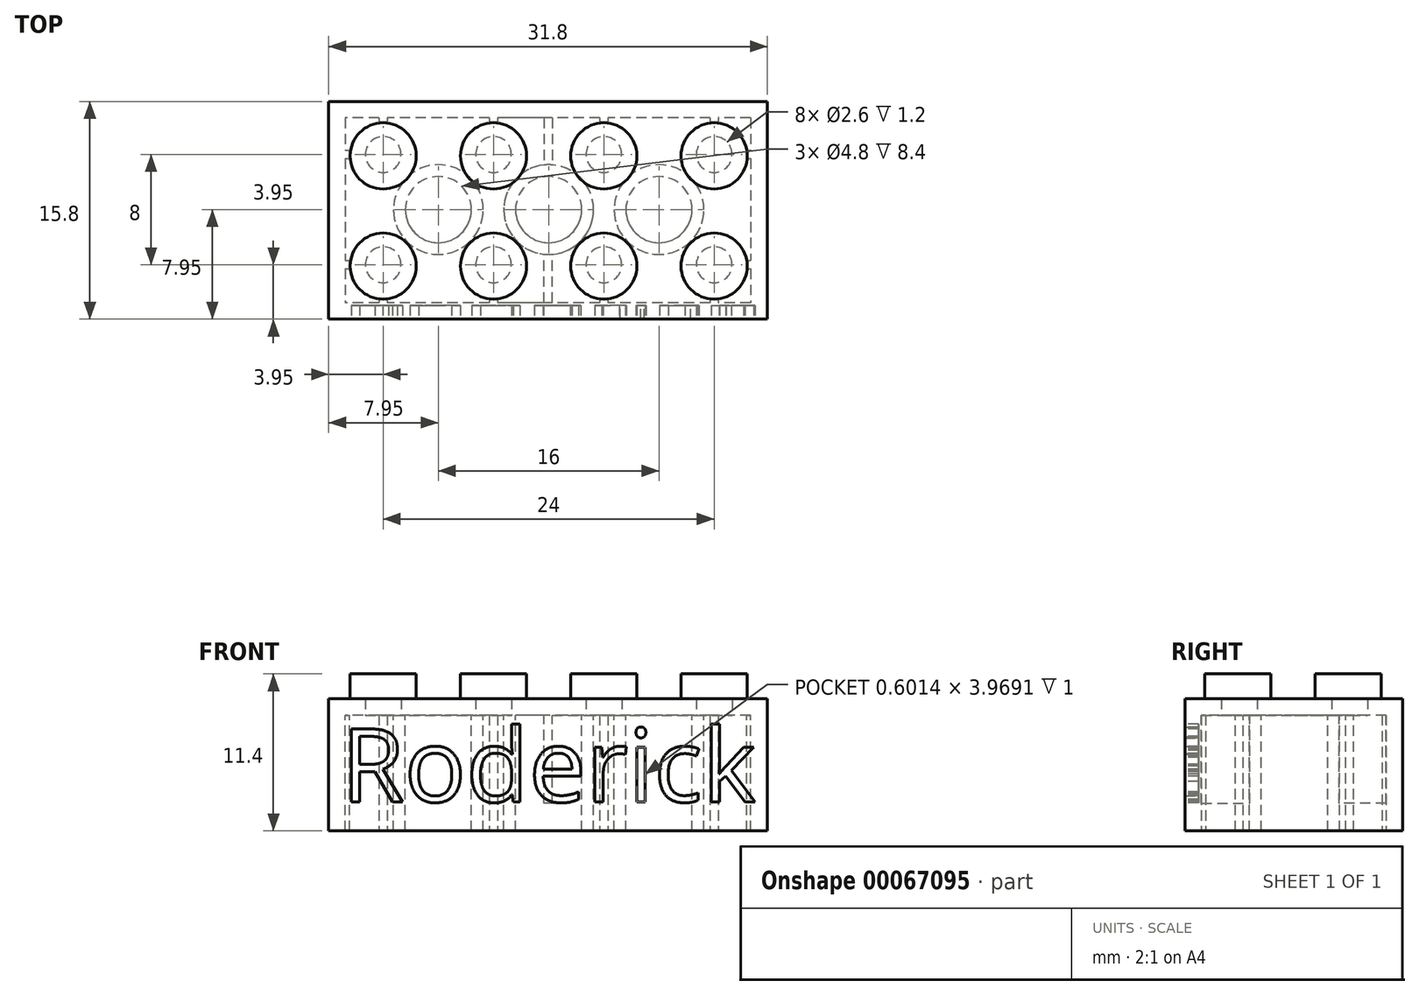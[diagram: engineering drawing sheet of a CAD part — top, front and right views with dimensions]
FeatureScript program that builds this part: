
annotation { "Feature Type Name" : "Feature", "Feature Type Description" : "" }
export const myFeature = defineFeature(function(context is Context, id is Id, definition is map)
    precondition{}
    {
        {
            var Q0;
            Q0=qCreatedBy(makeId("Top.planeOp"),FACE);
            var sketch = newSketch(context, id + "F0", { "sketchPlane" : qUnion([Q0])});
            skLineSegment(sketch, "E0.rect.bottom", {"start": v(15.9, -7.9) * mm, "end": v(-15.9, -7.9) * mm});
            skLineSegment(sketch, "E0.rect.top", {"start": v(15.9, 7.9) * mm, "end": v(-15.9, 7.9) * mm});
            skLineSegment(sketch, "E0.rect.left", {"start": v(15.9, -7.9) * mm, "end": v(15.9, 7.9) * mm});
            skLineSegment(sketch, "E0.rect.right", {"start": v(-15.9, -7.9) * mm, "end": v(-15.9, 7.9) * mm});
            skPoint(sketch, "E0.rect.middle", {"position": v(0, 0) * mm});
            skSolve(sketch);
        }
        {
            var Q0;
            Q0 = qSketchRegion(id + "F0", true);
            extrude(context, id + "F1", {"entities" : qUnion([Q0]), "depth" : 9.6 * mm});
        }
        {
            var Q0;
            Q0=makeQuery(id+"F1.opExtrude","CAP_FACE",FACE,{"disambiguationData":[OSD([sQuery(id+"F0.wireOp",EDGE,"E0.rect.bottom"),sQuery(id+"F0.wireOp",EDGE,"E0.rect.top"),sQuery(id+"F0.wireOp",EDGE,"E0.rect.left"),sQuery(id+"F0.wireOp",EDGE,"E0.rect.right")])],"isStart":true});
            var sketch = newSketch(context, id + "F2", { "sketchPlane" : qUnion([Q0])});
            skLineSegment(sketch, "E1.rect.bottom", {"start": v(14.7, -6.7) * mm, "end": v(-14.7, -6.7) * mm});
            skLineSegment(sketch, "E1.rect.top", {"start": v(14.7, 6.7) * mm, "end": v(-14.7, 6.7) * mm});
            skLineSegment(sketch, "E1.rect.left", {"start": v(14.7, -6.7) * mm, "end": v(14.7, 6.7) * mm});
            skLineSegment(sketch, "E1.rect.right", {"start": v(-14.7, -6.7) * mm, "end": v(-14.7, 6.7) * mm});
            skPoint(sketch, "E1.rect.middle", {"position": v(0, 0) * mm});
            skSolve(sketch);
        }
        {
            var Q0;
            Q0 = qSketchRegion(id + "F2", true);
            var Q1;
            Q1 = qSketchRegion(id + "F8", true);
            extrude(context, id + "F3", {"entities" : qUnion([Q0, Q1]), "operationType" : NewBodyOperationType.REMOVE, "oppositeDirection" : true, "depth" : 8.4 * mm});
        }
        {
            var Q0;
            Q0=makeQuery(id+"F1.opExtrude","CAP_FACE",FACE,{"disambiguationData":[OSD([sQuery(id+"F0.wireOp",EDGE,"E0.rect.bottom"),sQuery(id+"F0.wireOp",EDGE,"E0.rect.top"),sQuery(id+"F0.wireOp",EDGE,"E0.rect.left"),sQuery(id+"F0.wireOp",EDGE,"E0.rect.right")])],"isStart":false});
            var sketch = newSketch(context, id + "F4", { "sketchPlane" : qUnion([Q0])});
            skLineSegment(sketch, "E2", {"start": v(-30.02, 0) * mm, "end": v(25.7, 0) * mm, "construction": true});
            skCircle(sketch, "E3", {"center": v(-11.95, 3.95) * mm, "radius": 2.4 * mm});
            skCircle(sketch, "E4.0.1.0", {"center": v(-11.95, -4.05) * mm, "radius": 2.4 * mm});
            skCircle(sketch, "E4.1.0.0", {"center": v(-3.95, 3.95) * mm, "radius": 2.4 * mm});
            skCircle(sketch, "E4.1.1.0", {"center": v(-3.95, -4.05) * mm, "radius": 2.4 * mm});
            skCircle(sketch, "E4.2.0.0", {"center": v(4.05, 3.95) * mm, "radius": 2.4 * mm});
            skCircle(sketch, "E4.2.1.0", {"center": v(4.05, -4.05) * mm, "radius": 2.4 * mm});
            skCircle(sketch, "E4.3.0.0", {"center": v(12.05, 3.95) * mm, "radius": 2.4 * mm});
            skCircle(sketch, "E4.3.1.0", {"center": v(12.05, -4.05) * mm, "radius": 2.4 * mm});
            skLineSegment(sketch, "E4.direction1", {"start": v(-11.95, 3.95) * mm, "end": v(-3.95, 3.95) * mm, "construction": true});
            skLineSegment(sketch, "E4.direction2", {"start": v(-11.95, 3.95) * mm, "end": v(-11.95, -4.05) * mm, "construction": true});
            skSolve(sketch);
        }
        {
            var Q0;
            Q0=makeQuery(id+"F4.imprint","IMPRINT",FACE,{"disambiguationData":[TD([[makeQuery(id+"F4.imprint","IMPRINT",EDGE,{"derivedFrom":sQuery(id+"F4.wireOp",EDGE,"E3")}),1.0]])]});
            var Q1;
            Q1=makeQuery(id+"F4.imprint","IMPRINT",FACE,{"disambiguationData":[TD([[makeQuery(id+"F4.imprint","IMPRINT",EDGE,{"derivedFrom":sQuery(id+"F4.wireOp",EDGE,"E4.1.0.0")}),1.0]])]});
            var Q2;
            Q2=makeQuery(id+"F4.imprint","IMPRINT",FACE,{"disambiguationData":[TD([[makeQuery(id+"F4.imprint","IMPRINT",EDGE,{"derivedFrom":sQuery(id+"F4.wireOp",EDGE,"E4.2.0.0")}),1.0]])]});
            var Q3;
            Q3=makeQuery(id+"F4.imprint","IMPRINT",FACE,{"disambiguationData":[TD([[makeQuery(id+"F4.imprint","IMPRINT",EDGE,{"derivedFrom":sQuery(id+"F4.wireOp",EDGE,"E4.3.0.0")}),1.0]])]});
            var Q4;
            Q4=makeQuery(id+"F4.imprint","IMPRINT",FACE,{"disambiguationData":[TD([[makeQuery(id+"F4.imprint","IMPRINT",EDGE,{"derivedFrom":sQuery(id+"F4.wireOp",EDGE,"E4.3.1.0")}),1.0]])]});
            var Q5;
            Q5=makeQuery(id+"F4.imprint","IMPRINT",FACE,{"disambiguationData":[TD([[makeQuery(id+"F4.imprint","IMPRINT",EDGE,{"derivedFrom":sQuery(id+"F4.wireOp",EDGE,"E4.2.1.0")}),1.0]])]});
            var Q6;
            Q6=makeQuery(id+"F4.imprint","IMPRINT",FACE,{"disambiguationData":[TD([[makeQuery(id+"F4.imprint","IMPRINT",EDGE,{"derivedFrom":sQuery(id+"F4.wireOp",EDGE,"E4.1.1.0")}),1.0]])]});
            var Q7;
            Q7=makeQuery(id+"F4.imprint","IMPRINT",FACE,{"disambiguationData":[TD([[makeQuery(id+"F4.imprint","IMPRINT",EDGE,{"derivedFrom":sQuery(id+"F4.wireOp",EDGE,"E4.0.1.0")}),1.0]])]});
            extrude(context, id + "F5", {"entities" : qUnion([Q0, Q1, Q2, Q3, Q4, Q5, Q6, Q7]), "operationType" : NewBodyOperationType.ADD, "depth" : 1.8 * mm});
        }
        {
            var Q0;
            Q0=makeQuery(id+"F3.boolean.opBoolean","COPY",FACE,{"derivedFrom":makeQuery(id+"F3.opExtrude","CAP_FACE",FACE,{"disambiguationData":[OSD([sQuery(id+"F2.wireOp",EDGE,"E1.rect.bottom"),sQuery(id+"F2.wireOp",EDGE,"E1.rect.top"),sQuery(id+"F2.wireOp",EDGE,"E1.rect.left"),sQuery(id+"F2.wireOp",EDGE,"E1.rect.right")])],"isStart":false})});
            var sketch = newSketch(context, id + "F6", { "sketchPlane" : qUnion([Q0])});
            skCircle(sketch, "E5", {"center": v(-11.95, 3.95) * mm, "radius": 1.3 * mm});
            skCircle(sketch, "E6.0.1.0", {"center": v(-11.95, -4.05) * mm, "radius": 1.3 * mm});
            skCircle(sketch, "E6.1.0.0", {"center": v(-3.95, 3.95) * mm, "radius": 1.3 * mm});
            skCircle(sketch, "E6.1.1.0", {"center": v(-3.95, -4.05) * mm, "radius": 1.3 * mm});
            skCircle(sketch, "E6.2.0.0", {"center": v(4.05, 3.95) * mm, "radius": 1.3 * mm});
            skCircle(sketch, "E6.2.1.0", {"center": v(4.05, -4.05) * mm, "radius": 1.3 * mm});
            skCircle(sketch, "E6.3.0.0", {"center": v(12.05, 3.95) * mm, "radius": 1.3 * mm});
            skCircle(sketch, "E6.3.1.0", {"center": v(12.05, -4.05) * mm, "radius": 1.3 * mm});
            skLineSegment(sketch, "E6.direction1", {"start": v(-11.95, 3.95) * mm, "end": v(-3.95, 3.95) * mm, "construction": true});
            skLineSegment(sketch, "E6.direction2", {"start": v(-11.95, 3.95) * mm, "end": v(-11.95, -4.05) * mm, "construction": true});
            skSolve(sketch);
        }
        {
            var Q0;
            Q0 = qSketchRegion(id + "F6", true);
            extrude(context, id + "F7", {"entities" : qUnion([Q0]), "operationType" : NewBodyOperationType.REMOVE, "oppositeDirection" : true, "depth" : 1.2 * mm});
        }
        {
            var Q0;
            Q0=makeQuery(id+"F3.boolean.opBoolean","COPY",FACE,{"derivedFrom":makeQuery(id+"F3.opExtrude","CAP_FACE",FACE,{"disambiguationData":[OSD([sQuery(id+"F2.wireOp",EDGE,"E1.rect.bottom"),sQuery(id+"F2.wireOp",EDGE,"E1.rect.top"),sQuery(id+"F2.wireOp",EDGE,"E1.rect.left"),sQuery(id+"F2.wireOp",EDGE,"E1.rect.right")])],"isStart":false})});
            var sketch = newSketch(context, id + "F8", { "sketchPlane" : qUnion([Q0])});
            skLineSegment(sketch, "E7", {"start": v(-11.95, 3.95) * mm, "end": v(-3.95, -4.05) * mm, "construction": true});
            skLineSegment(sketch, "E8", {"start": v(-3.95, 3.95) * mm, "end": v(-11.95, -4.05) * mm, "construction": true});
            skLineSegment(sketch, "E9", {"start": v(4.05, 3.95) * mm, "end": v(-3.95, -4.05) * mm, "construction": true});
            skLineSegment(sketch, "E10", {"start": v(-3.95, 3.95) * mm, "end": v(4.05, -4.05) * mm, "construction": true});
            skLineSegment(sketch, "E11", {"start": v(4.05, 3.95) * mm, "end": v(12.05, -4.05) * mm, "construction": true});
            skLineSegment(sketch, "E12", {"start": v(12.05, 3.95) * mm, "end": v(4.05, -4.05) * mm, "construction": true});
            skPoint(sketch, "E13", {"position": v(-7.95, -0.05) * mm});
            skPoint(sketch, "E14", {"position": v(0, 0) * mm});
            skPoint(sketch, "E15", {"position": v(8.05, -0.05) * mm});
            skCircle(sketch, "E16", {"center": v(-7.95, -0.05) * mm, "radius": 3.25 * mm});
            skCircle(sketch, "E17.1.0.0", {"center": v(0.05, -0.05) * mm, "radius": 3.25 * mm});
            skCircle(sketch, "E17.2.0.0", {"center": v(8.05, -0.05) * mm, "radius": 3.25 * mm});
            skLineSegment(sketch, "E17.direction1", {"start": v(-7.95, -0.05) * mm, "end": v(0.05, -0.05) * mm, "construction": true});
            skCircle(sketch, "E18", {"center": v(-7.95, -0.05) * mm, "radius": 2.4 * mm});
            skCircle(sketch, "E19.1.0.0", {"center": v(0.05, -0.05) * mm, "radius": 2.4 * mm});
            skCircle(sketch, "E19.2.0.0", {"center": v(8.05, -0.05) * mm, "radius": 2.4 * mm});
            skSolve(sketch);
        }
        {
            var Q0;
            Q0 = qSketchRegion(id + "F8", true);
            var Q1;
            Q1=makeQuery(id+"F1.opExtrude","CAP_FACE",FACE,{"disambiguationData":[OSD([sQuery(id+"F0.wireOp",EDGE,"E0.rect.bottom"),sQuery(id+"F0.wireOp",EDGE,"E0.rect.top"),sQuery(id+"F0.wireOp",EDGE,"E0.rect.left"),sQuery(id+"F0.wireOp",EDGE,"E0.rect.right")])],"isStart":true});
            extrude(context, id + "F9", {"entities" : qUnion([Q0]), "operationType" : NewBodyOperationType.ADD, "endBound" : BoundingType.UP_TO_SURFACE, "endBoundEntityFace" : qUnion([Q1]), "depth" : 25 * mm});
        }
        {
            var Q0;
            Q0=makeQuery(id+"F1.opExtrude","CAP_FACE",FACE,{"disambiguationData":[OSD([sQuery(id+"F0.wireOp",EDGE,"E0.rect.bottom"),sQuery(id+"F0.wireOp",EDGE,"E0.rect.top"),sQuery(id+"F0.wireOp",EDGE,"E0.rect.left"),sQuery(id+"F0.wireOp",EDGE,"E0.rect.right")])],"isStart":true});
            var sketch = newSketch(context, id + "F10", { "sketchPlane" : qUnion([Q0])});
            skLineSegment(sketch, "E20.bottom", {"start": v(-12.25, 6.7) * mm, "end": v(-11.65, 6.7) * mm});
            skLineSegment(sketch, "E20.top", {"start": v(-12.25, 6.4) * mm, "end": v(-11.65, 6.4) * mm});
            skLineSegment(sketch, "E20.left", {"start": v(-12.25, 6.7) * mm, "end": v(-12.25, 6.4) * mm});
            skLineSegment(sketch, "E20.right", {"start": v(-11.65, 6.7) * mm, "end": v(-11.65, 6.4) * mm});
            skLineSegment(sketch, "E21", {"start": v(-11.95, -4.05) * mm, "end": v(-11.95, 15.06) * mm, "construction": true});
            skLineSegment(sketch, "E22.0.1.0", {"start": v(-12.25, -6.4) * mm, "end": v(-11.65, -6.4) * mm});
            skLineSegment(sketch, "E22.0.1.1", {"start": v(-12.25, -6.4) * mm, "end": v(-12.25, -6.7) * mm});
            skLineSegment(sketch, "E22.0.1.2", {"start": v(-12.25, -6.7) * mm, "end": v(-11.65, -6.7) * mm});
            skLineSegment(sketch, "E22.0.1.3", {"start": v(-11.65, -6.4) * mm, "end": v(-11.65, -6.7) * mm});
            skLineSegment(sketch, "E22.1.0.0", {"start": v(-4.25, 6.7) * mm, "end": v(-3.65, 6.7) * mm});
            skLineSegment(sketch, "E22.1.0.1", {"start": v(-4.25, 6.7) * mm, "end": v(-4.25, 6.4) * mm});
            skLineSegment(sketch, "E22.1.0.2", {"start": v(-4.25, 6.4) * mm, "end": v(-3.65, 6.4) * mm});
            skLineSegment(sketch, "E22.1.0.3", {"start": v(-3.65, 6.7) * mm, "end": v(-3.65, 6.4) * mm});
            skLineSegment(sketch, "E22.1.1.0", {"start": v(-4.25, -6.4) * mm, "end": v(-3.65, -6.4) * mm});
            skLineSegment(sketch, "E22.1.1.1", {"start": v(-4.25, -6.4) * mm, "end": v(-4.25, -6.7) * mm});
            skLineSegment(sketch, "E22.1.1.2", {"start": v(-4.25, -6.7) * mm, "end": v(-3.65, -6.7) * mm});
            skLineSegment(sketch, "E22.1.1.3", {"start": v(-3.65, -6.4) * mm, "end": v(-3.65, -6.7) * mm});
            skLineSegment(sketch, "E22.2.0.0", {"start": v(3.75, 6.7) * mm, "end": v(4.35, 6.7) * mm});
            skLineSegment(sketch, "E22.2.0.1", {"start": v(3.75, 6.7) * mm, "end": v(3.75, 6.4) * mm});
            skLineSegment(sketch, "E22.2.0.2", {"start": v(3.75, 6.4) * mm, "end": v(4.35, 6.4) * mm});
            skLineSegment(sketch, "E22.2.0.3", {"start": v(4.35, 6.7) * mm, "end": v(4.35, 6.4) * mm});
            skLineSegment(sketch, "E22.2.1.0", {"start": v(3.75, -6.4) * mm, "end": v(4.35, -6.4) * mm});
            skLineSegment(sketch, "E22.2.1.1", {"start": v(3.75, -6.4) * mm, "end": v(3.75, -6.7) * mm});
            skLineSegment(sketch, "E22.2.1.2", {"start": v(3.75, -6.7) * mm, "end": v(4.35, -6.7) * mm});
            skLineSegment(sketch, "E22.2.1.3", {"start": v(4.35, -6.4) * mm, "end": v(4.35, -6.7) * mm});
            skLineSegment(sketch, "E22.3.0.0", {"start": v(11.75, 6.7) * mm, "end": v(12.35, 6.7) * mm});
            skLineSegment(sketch, "E22.3.0.1", {"start": v(11.75, 6.7) * mm, "end": v(11.75, 6.4) * mm});
            skLineSegment(sketch, "E22.3.0.2", {"start": v(11.75, 6.4) * mm, "end": v(12.35, 6.4) * mm});
            skLineSegment(sketch, "E22.3.0.3", {"start": v(12.35, 6.7) * mm, "end": v(12.35, 6.4) * mm});
            skLineSegment(sketch, "E22.3.1.0", {"start": v(11.75, -6.4) * mm, "end": v(12.35, -6.4) * mm});
            skLineSegment(sketch, "E22.3.1.1", {"start": v(11.75, -6.4) * mm, "end": v(11.75, -6.7) * mm});
            skLineSegment(sketch, "E22.3.1.2", {"start": v(11.75, -6.7) * mm, "end": v(12.35, -6.7) * mm});
            skLineSegment(sketch, "E22.3.1.3", {"start": v(12.35, -6.4) * mm, "end": v(12.35, -6.7) * mm});
            skLineSegment(sketch, "E22.direction1", {"start": v(-12.25, 6.7) * mm, "end": v(-4.25, 6.7) * mm, "construction": true});
            skLineSegment(sketch, "E22.direction2", {"start": v(-12.25, 6.7) * mm, "end": v(-12.25, -6.4) * mm, "construction": true});
            skSolve(sketch);
        }
        {
            var Q0;
            Q0 = qSketchRegion(id + "F10", true);
            var Q1;
            {var subQ0=sQuery(id+"F2.wireOp",EDGE,"E1.rect.bottom");var subQ1=sQuery(id+"F2.wireOp",EDGE,"E1.rect.top");var subQ2=sQuery(id+"F2.wireOp",EDGE,"E1.rect.left");var subQ3=sQuery(id+"F2.wireOp",EDGE,"E1.rect.right");Q1=makeQuery(id+"F9.boolean.opBoolean","SPLIT",FACE,{"disambiguationData":[TD([makeQuery(id+"F3.boolean.opBoolean","COPY",FACE,{"derivedFrom":makeQuery(id+"F3.opExtrude","SWEPT_FACE",FACE,{"disambiguationData":[OSD([subQ0])]})})])],"derivedFrom":makeQuery(id+"F3.boolean.opBoolean","COPY",FACE,{"derivedFrom":makeQuery(id+"F3.opExtrude","CAP_FACE",FACE,{"disambiguationData":[OSD([subQ0,subQ1,subQ2,subQ3])],"isStart":false})})});}
            extrude(context, id + "F11", {"entities" : qUnion([Q0]), "operationType" : NewBodyOperationType.ADD, "endBound" : BoundingType.UP_TO_SURFACE, "oppositeDirection" : true, "endBoundEntityFace" : qUnion([Q1]), "depth" : 25 * mm});
        }
        {
            var Q0;
            {var subQ0=sQuery(id+"F2.wireOp",EDGE,"E1.rect.bottom");var subQ1=sQuery(id+"F2.wireOp",EDGE,"E1.rect.top");var subQ2=sQuery(id+"F2.wireOp",EDGE,"E1.rect.left");var subQ3=sQuery(id+"F2.wireOp",EDGE,"E1.rect.right");Q0=makeQuery(id+"F9.boolean.opBoolean","SPLIT",FACE,{"disambiguationData":[TD([makeQuery(id+"F3.boolean.opBoolean","COPY",FACE,{"derivedFrom":makeQuery(id+"F3.opExtrude","SWEPT_FACE",FACE,{"disambiguationData":[OSD([subQ0])]})})])],"derivedFrom":makeQuery(id+"F3.boolean.opBoolean","COPY",FACE,{"derivedFrom":makeQuery(id+"F3.opExtrude","CAP_FACE",FACE,{"disambiguationData":[OSD([subQ0,subQ1,subQ2,subQ3])],"isStart":false})})});}
            var sketch = newSketch(context, id + "F12", { "sketchPlane" : qUnion([Q0])});
            skLineSegment(sketch, "E23", {"start": v(-11.95, 3.95) * mm, "end": v(-16.94, 3.95) * mm, "construction": true});
            skLineSegment(sketch, "E24.bottom", {"start": v(-14.7, 4.25) * mm, "end": v(-14.4, 4.25) * mm});
            skLineSegment(sketch, "E24.top", {"start": v(-14.7, 3.65) * mm, "end": v(-14.4, 3.65) * mm});
            skLineSegment(sketch, "E24.left", {"start": v(-14.7, 4.25) * mm, "end": v(-14.7, 3.65) * mm});
            skLineSegment(sketch, "E24.right", {"start": v(-14.4, 4.25) * mm, "end": v(-14.4, 3.65) * mm});
            skLineSegment(sketch, "E25.0.1.0", {"start": v(-14.7, -3.75) * mm, "end": v(-14.4, -3.75) * mm});
            skLineSegment(sketch, "E25.0.1.1", {"start": v(-14.4, -3.75) * mm, "end": v(-14.4, -4.35) * mm});
            skLineSegment(sketch, "E25.0.1.2", {"start": v(-14.7, -4.35) * mm, "end": v(-14.4, -4.35) * mm});
            skLineSegment(sketch, "E25.0.1.3", {"start": v(-14.7, -3.75) * mm, "end": v(-14.7, -4.35) * mm});
            skLineSegment(sketch, "E25.1.0.0", {"start": v(14.4, 4.25) * mm, "end": v(14.7, 4.25) * mm});
            skLineSegment(sketch, "E25.1.0.1", {"start": v(14.7, 4.25) * mm, "end": v(14.7, 3.65) * mm});
            skLineSegment(sketch, "E25.1.0.2", {"start": v(14.4, 3.65) * mm, "end": v(14.7, 3.65) * mm});
            skLineSegment(sketch, "E25.1.0.3", {"start": v(14.4, 4.25) * mm, "end": v(14.4, 3.65) * mm});
            skLineSegment(sketch, "E25.1.1.0", {"start": v(14.4, -3.75) * mm, "end": v(14.7, -3.75) * mm});
            skLineSegment(sketch, "E25.1.1.1", {"start": v(14.7, -3.75) * mm, "end": v(14.7, -4.35) * mm});
            skLineSegment(sketch, "E25.1.1.2", {"start": v(14.4, -4.35) * mm, "end": v(14.7, -4.35) * mm});
            skLineSegment(sketch, "E25.1.1.3", {"start": v(14.4, -3.75) * mm, "end": v(14.4, -4.35) * mm});
            skLineSegment(sketch, "E25.direction1", {"start": v(-14.7, 4.25) * mm, "end": v(14.4, 4.25) * mm, "construction": true});
            skLineSegment(sketch, "E25.direction2", {"start": v(-14.7, 4.25) * mm, "end": v(-14.7, -3.75) * mm, "construction": true});
            skSolve(sketch);
        }
        {
            var Q0;
            Q0 = qSketchRegion(id + "F12", true);
            var Q1;
            Q1=makeQuery(id+"F11.boolean.opBoolean","MERGE",FACE,{"derivedFrom":[makeQuery(id+"F1.opExtrude","CAP_FACE",FACE,{"disambiguationData":[OSD([sQuery(id+"F0.wireOp",EDGE,"E0.rect.bottom"),sQuery(id+"F0.wireOp",EDGE,"E0.rect.top"),sQuery(id+"F0.wireOp",EDGE,"E0.rect.left"),sQuery(id+"F0.wireOp",EDGE,"E0.rect.right")])],"isStart":true}),makeQuery(id+"F11.opExtrude","CAP_FACE",FACE,{"disambiguationData":[OSD([sQuery(id+"F10.wireOp",EDGE,"E20.bottom"),sQuery(id+"F10.wireOp",EDGE,"E20.top"),sQuery(id+"F10.wireOp",EDGE,"E20.left"),sQuery(id+"F10.wireOp",EDGE,"E20.right")])],"isStart":true}),makeQuery(id+"F11.opExtrude","CAP_FACE",FACE,{"disambiguationData":[OSD([sQuery(id+"F10.wireOp",EDGE,"E22.0.1.0"),sQuery(id+"F10.wireOp",EDGE,"E22.0.1.1"),sQuery(id+"F10.wireOp",EDGE,"E22.0.1.2"),sQuery(id+"F10.wireOp",EDGE,"E22.0.1.3")])],"isStart":true}),makeQuery(id+"F11.opExtrude","CAP_FACE",FACE,{"disambiguationData":[OSD([sQuery(id+"F10.wireOp",EDGE,"E22.1.0.0"),sQuery(id+"F10.wireOp",EDGE,"E22.1.0.1"),sQuery(id+"F10.wireOp",EDGE,"E22.1.0.2"),sQuery(id+"F10.wireOp",EDGE,"E22.1.0.3")])],"isStart":true}),makeQuery(id+"F11.opExtrude","CAP_FACE",FACE,{"disambiguationData":[OSD([sQuery(id+"F10.wireOp",EDGE,"E22.1.1.0"),sQuery(id+"F10.wireOp",EDGE,"E22.1.1.1"),sQuery(id+"F10.wireOp",EDGE,"E22.1.1.2"),sQuery(id+"F10.wireOp",EDGE,"E22.1.1.3")])],"isStart":true}),makeQuery(id+"F11.opExtrude","CAP_FACE",FACE,{"disambiguationData":[OSD([sQuery(id+"F10.wireOp",EDGE,"E22.2.0.0"),sQuery(id+"F10.wireOp",EDGE,"E22.2.0.1"),sQuery(id+"F10.wireOp",EDGE,"E22.2.0.2"),sQuery(id+"F10.wireOp",EDGE,"E22.2.0.3")])],"isStart":true}),makeQuery(id+"F11.opExtrude","CAP_FACE",FACE,{"disambiguationData":[OSD([sQuery(id+"F10.wireOp",EDGE,"E22.2.1.0"),sQuery(id+"F10.wireOp",EDGE,"E22.2.1.1"),sQuery(id+"F10.wireOp",EDGE,"E22.2.1.2"),sQuery(id+"F10.wireOp",EDGE,"E22.2.1.3")])],"isStart":true}),makeQuery(id+"F11.opExtrude","CAP_FACE",FACE,{"disambiguationData":[OSD([sQuery(id+"F10.wireOp",EDGE,"E22.3.0.0"),sQuery(id+"F10.wireOp",EDGE,"E22.3.0.1"),sQuery(id+"F10.wireOp",EDGE,"E22.3.0.2"),sQuery(id+"F10.wireOp",EDGE,"E22.3.0.3")])],"isStart":true}),makeQuery(id+"F11.opExtrude","CAP_FACE",FACE,{"disambiguationData":[OSD([sQuery(id+"F10.wireOp",EDGE,"E22.3.1.0"),sQuery(id+"F10.wireOp",EDGE,"E22.3.1.1"),sQuery(id+"F10.wireOp",EDGE,"E22.3.1.2"),sQuery(id+"F10.wireOp",EDGE,"E22.3.1.3")])],"isStart":true})]});
            extrude(context, id + "F13", {"entities" : qUnion([Q0]), "operationType" : NewBodyOperationType.ADD, "endBound" : BoundingType.UP_TO_SURFACE, "endBoundEntityFace" : qUnion([Q1]), "depth" : 25 * mm});
        }
        {
            var Q0;
            {var subQ0=sQuery(id+"F2.wireOp",EDGE,"E1.rect.bottom");var subQ1=sQuery(id+"F2.wireOp",EDGE,"E1.rect.top");var subQ2=sQuery(id+"F2.wireOp",EDGE,"E1.rect.left");var subQ3=sQuery(id+"F2.wireOp",EDGE,"E1.rect.right");Q0=makeQuery(id+"F9.boolean.opBoolean","SPLIT",FACE,{"disambiguationData":[TD([makeQuery(id+"F3.boolean.opBoolean","COPY",FACE,{"derivedFrom":makeQuery(id+"F3.opExtrude","SWEPT_FACE",FACE,{"disambiguationData":[OSD([subQ0])]})})])],"derivedFrom":makeQuery(id+"F3.boolean.opBoolean","COPY",FACE,{"derivedFrom":makeQuery(id+"F3.opExtrude","CAP_FACE",FACE,{"disambiguationData":[OSD([subQ0,subQ1,subQ2,subQ3])],"isStart":false})})});}
            var sketch = newSketch(context, id + "F14", { "sketchPlane" : qUnion([Q0])});
            skLineSegment(sketch, "E26.bottom", {"start": v(-0.3, 6.7) * mm, "end": v(0.3, 6.7) * mm});
            skLineSegment(sketch, "E26.top", {"start": v(-0.3, 2.7) * mm, "end": v(0.3, 2.7) * mm});
            skLineSegment(sketch, "E26.left", {"start": v(-0.3, 6.7) * mm, "end": v(-0.3, 2.7) * mm});
            skLineSegment(sketch, "E26.right", {"start": v(0.3, 6.7) * mm, "end": v(0.3, 2.7) * mm});
            skLineSegment(sketch, "E27.bottom", {"start": v(0.3, -6.7) * mm, "end": v(-0.3, -6.7) * mm});
            skLineSegment(sketch, "E27.top", {"start": v(0.3, -2.7) * mm, "end": v(-0.3, -2.7) * mm});
            skLineSegment(sketch, "E27.left", {"start": v(0.3, -6.7) * mm, "end": v(0.3, -2.7) * mm});
            skLineSegment(sketch, "E27.right", {"start": v(-0.3, -6.7) * mm, "end": v(-0.3, -2.7) * mm});
            skSolve(sketch);
        }
        {
            var Q0;
            Q0 = qSketchRegion(id + "F14", true);
            extrude(context, id + "F15", {"entities" : qUnion([Q0]), "operationType" : NewBodyOperationType.ADD, "depth" : 6.4 * mm});
        }
        {
            var Q0;
            Q0=makeQuery(id+"F1.opExtrude","SWEPT_FACE",FACE,{"disambiguationData":[OSD([sQuery(id+"F0.wireOp",EDGE,"E0.rect.bottom")])]});
            var sketch = newSketch(context, id + "F16", { "sketchPlane" : qUnion([Q0])});
            skText(sketch, "E28", { "text": "Roderick\n", "fontName": "OpenSans-Regular.ttf"});
            const initialGuessF16  = {"E28": [-0.015, 0.00211, 1, 0, 0.00534]};
            skSetInitialGuess(sketch, initialGuessF16);
            skSolve(sketch);
        }
        {
            var Q0;
            Q0 = qSketchRegion(id + "F16", true);
            extrude(context, id + "F17", {"entities" : qUnion([Q0]), "operationType" : NewBodyOperationType.REMOVE, "oppositeDirection" : true, "depth" : 1 * mm});
        }
    });
